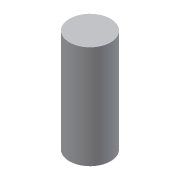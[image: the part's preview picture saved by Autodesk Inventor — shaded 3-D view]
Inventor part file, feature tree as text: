
AUTODESK INVENTOR PART (.ipt)
format: ipt  version: 2014 (Build 180170000, 170)  size: 63,488 bytes
history: native  units: mm
features: extrude x1, sketch x1
ambient origin geometry x8: Origin, YZ Plane, XZ Plane, XY Plane, X Axis, Y Axis, Z Axis, Center Point
bodies: Solid1 (feature_tree)
feature tree (2):
  extrude  "Extrusion1"  Depth=50.0mm TaperAngle=0.0deg
  sketch  "Sketch1"  dims[d0=20.0mm d1=50.0mm d2=0.0mm]
